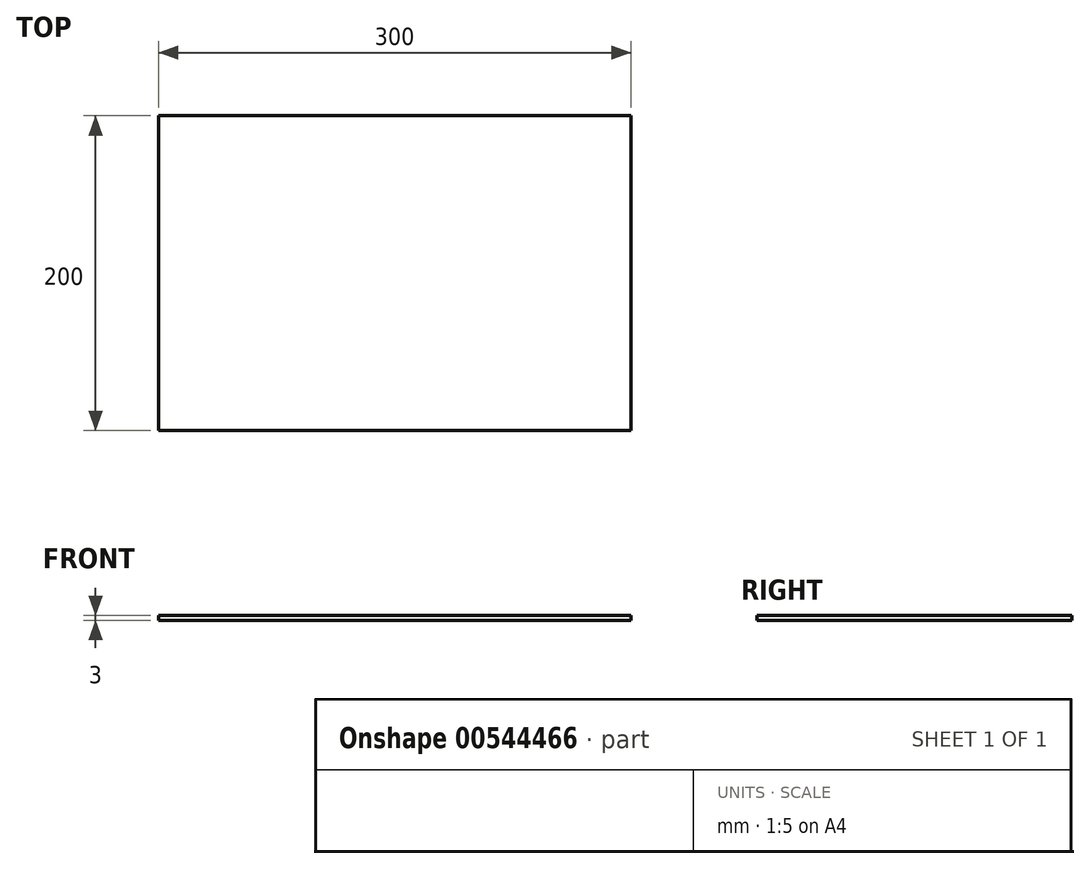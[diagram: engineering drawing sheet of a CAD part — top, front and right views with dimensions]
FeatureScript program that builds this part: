
annotation { "Feature Type Name" : "Feature", "Feature Type Description" : "" }
export const myFeature = defineFeature(function(context is Context, id is Id, definition is map)
    precondition{}
    {
        {
            var Q0;
            Q0=qCreatedBy(makeId("Top.planeOp"),FACE);
            var sketch = newSketch(context, id + "F0", { "sketchPlane" : qUnion([Q0])});
            skLineSegment(sketch, "E0.bottom", {"start": v(-150, -100) * mm, "end": v(150, -100) * mm});
            skLineSegment(sketch, "E0.top", {"start": v(-150, 100) * mm, "end": v(150, 100) * mm});
            skLineSegment(sketch, "E0.left", {"start": v(-150, -100) * mm, "end": v(-150, 100) * mm});
            skLineSegment(sketch, "E0.right", {"start": v(150, -100) * mm, "end": v(150, 100) * mm});
            skSolve(sketch);
        }
        {
            var Q0;
            Q0=makeQuery(id+"F0.imprint","IMPRINT",FACE,{"disambiguationData":[TD([[makeQuery(id+"F0.imprint","IMPRINT",EDGE,{"derivedFrom":sQuery(id+"F0.wireOp",EDGE,"E0.bottom")}),1.0]])]});
            extrude(context, id + "F1", {"entities" : qUnion([Q0]), "depth" : 3 * mm, "offsetDistance" : 25 * mm});
        }
    });
